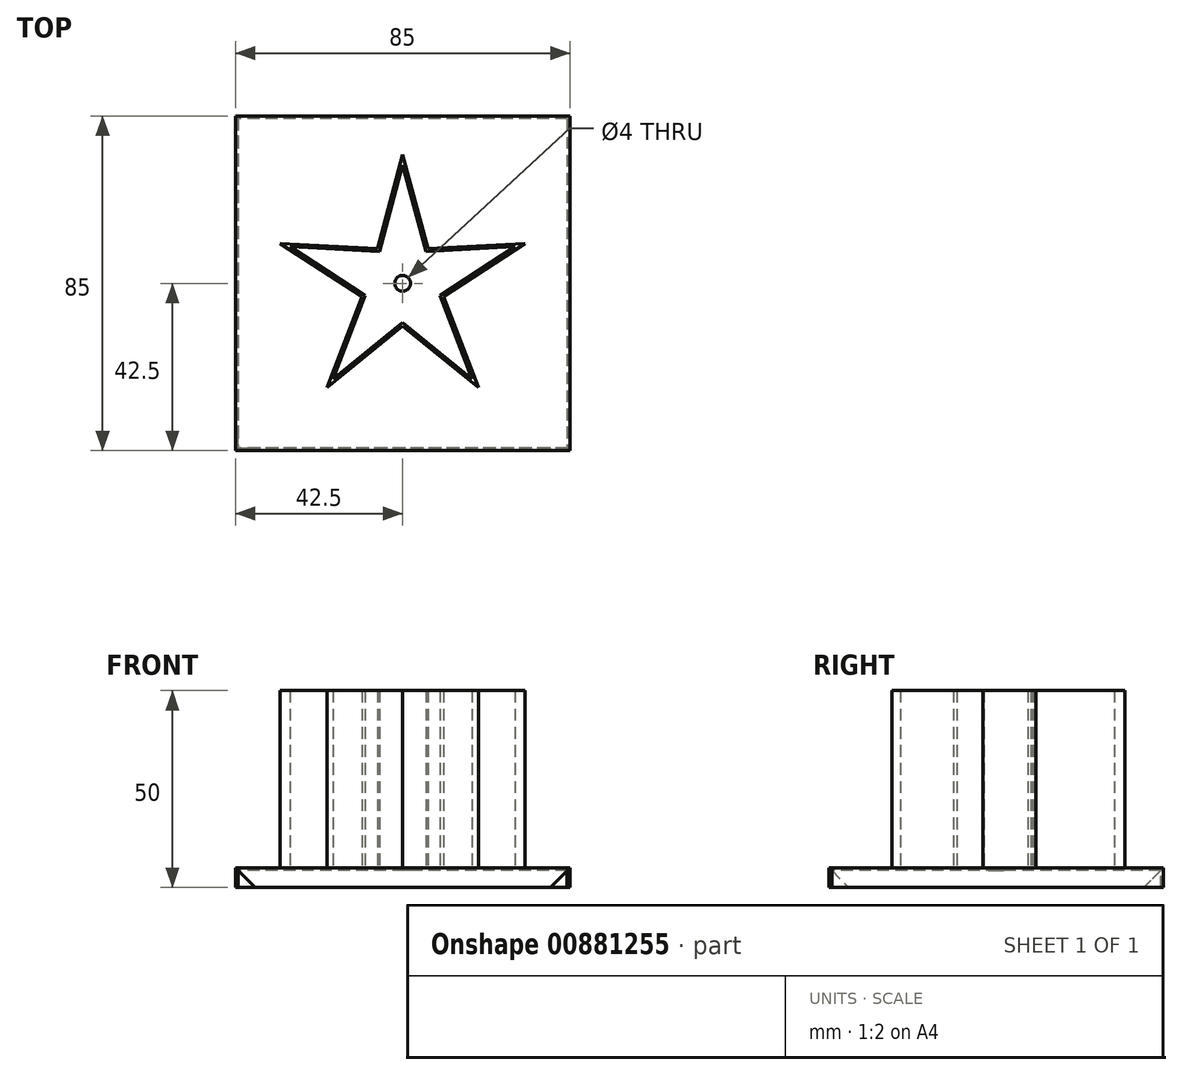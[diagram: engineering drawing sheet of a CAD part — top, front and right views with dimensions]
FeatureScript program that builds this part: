
annotation { "Feature Type Name" : "Feature", "Feature Type Description" : "" }
export const myFeature = defineFeature(function(context is Context, id is Id, definition is map)
    precondition{}
    {
        {
            var Q0;
            Q0=qCreatedBy(makeId("Top.planeOp"),FACE);
            var sketch = newSketch(context, id + "F0", { "sketchPlane" : qUnion([Q0])});
            skLineSegment(sketch, "E0.bottom", {"start": v(42.5, 42.5) * mm, "end": v(-42.5, 42.5) * mm});
            skLineSegment(sketch, "E0.top", {"start": v(42.5, -42.5) * mm, "end": v(-42.5, -42.5) * mm});
            skLineSegment(sketch, "E0.left", {"start": v(42.5, 42.5) * mm, "end": v(42.5, -42.5) * mm});
            skLineSegment(sketch, "E0.right", {"start": v(-42.5, 42.5) * mm, "end": v(-42.5, -42.5) * mm});
            skPoint(sketch, "E0.middle", {"position": v(0, 0) * mm});
            skCircle(sketch, "E1", {"center": v(0, 0) * mm, "radius": 2 * mm});
            skSolve(sketch);
        }
        {
            var Q0;
            Q0 = qSketchRegion(id + "F0", true);
            extrude(context, id + "F1", {"entities" : qUnion([Q0]), "depth" : 0.7 * mm, "offsetDistance" : 25 * mm});
        }
        {
            var Q0;
            Q0=makeQuery(id+"F1.opExtrude","CAP_FACE",FACE,{"disambiguationData":[OSD([sQuery(id+"F0.wireOp",EDGE,"E0.bottom"),sQuery(id+"F0.wireOp",EDGE,"E0.top"),sQuery(id+"F0.wireOp",EDGE,"E0.left"),sQuery(id+"F0.wireOp",EDGE,"E0.right"),sQuery(id+"F0.wireOp",EDGE,"E1")])],"isStart":false});
            var sketch = newSketch(context, id + "F2", { "sketchPlane" : qUnion([Q0])});
            skLineSegment(sketch, "E2", {"start": v(0, 30.03) * mm, "end": v(-5.88, 8.1) * mm});
            skLineSegment(sketch, "E3", {"start": v(-5.88, 8.1) * mm, "end": v(-28.56, 9.28) * mm});
            skLineSegment(sketch, "E4", {"start": v(-28.56, 9.28) * mm, "end": v(-9.51, -3.1) * mm});
            skLineSegment(sketch, "E5", {"start": v(-9.51, -3.1) * mm, "end": v(-17.65, -24.3) * mm});
            skCircle(sketch, "E6", {"center": v(0, 0) * mm, "radius": 10 * mm, "construction": true});
            skLineSegment(sketch, "E7", {"start": v(-17.65, -24.3) * mm, "end": v(0, -10) * mm});
            skLineSegment(sketch, "E8.MirrorCS", {"start": v(17.65, -24.3) * mm, "end": v(0, -10) * mm});
            skLineSegment(sketch, "E9.MirrorCS", {"start": v(9.51, -3.1) * mm, "end": v(17.65, -24.3) * mm});
            skLineSegment(sketch, "E10.MirrorCS", {"start": v(28.56, 9.28) * mm, "end": v(9.51, -3.1) * mm});
            skLineSegment(sketch, "E11.MirrorCS", {"start": v(0, 30.03) * mm, "end": v(5.88, 8.1) * mm});
            skLineSegment(sketch, "E12.MirrorCS", {"start": v(5.88, 8.1) * mm, "end": v(28.56, 9.28) * mm});
            skLineSegment(sketch, "E13.0", {"start": v(0, 32.73) * mm, "end": v(6.4, 8.82) * mm});
            skLineSegment(sketch, "E13.1", {"start": v(6.4, 8.82) * mm, "end": v(31.13, 10.11) * mm});
            skLineSegment(sketch, "E13.2", {"start": v(0, 32.73) * mm, "end": v(-6.4, 8.82) * mm});
            skLineSegment(sketch, "E13.3", {"start": v(31.13, 10.11) * mm, "end": v(10.37, -3.37) * mm});
            skLineSegment(sketch, "E13.4", {"start": v(10.37, -3.37) * mm, "end": v(19.24, -26.48) * mm});
            skLineSegment(sketch, "E13.5", {"start": v(19.24, -26.48) * mm, "end": v(0, -10.9) * mm});
            skLineSegment(sketch, "E13.6", {"start": v(-6.4, 8.82) * mm, "end": v(-31.13, 10.11) * mm});
            skLineSegment(sketch, "E13.7", {"start": v(-31.13, 10.11) * mm, "end": v(-10.37, -3.37) * mm});
            skLineSegment(sketch, "E13.8", {"start": v(-10.37, -3.37) * mm, "end": v(-19.24, -26.48) * mm});
            skLineSegment(sketch, "E13.9", {"start": v(-19.24, -26.48) * mm, "end": v(0, -10.9) * mm});
            skLineSegment(sketch, "E14", {"start": v(0, 0) * mm, "end": v(17.65, -24.3) * mm, "construction": true});
            skLineSegment(sketch, "E15", {"start": v(0, 0) * mm, "end": v(28.56, 9.28) * mm, "construction": true});
            skLineSegment(sketch, "E16", {"start": v(0, 0) * mm, "end": v(-17.65, -24.3) * mm, "construction": true});
            skLineSegment(sketch, "E17", {"start": v(0, 0) * mm, "end": v(-28.56, 9.28) * mm, "construction": true});
            skLineSegment(sketch, "E18", {"start": v(0, 0) * mm, "end": v(0, 30.03) * mm, "construction": true});
            skPoint(sketch, "E19.orphan", {"position": v(0, -10) * mm});
            skSolve(sketch);
        }
        {
            var Q0;
            Q0 = qSketchRegion(id + "F2", true);
            extrude(context, id + "F3", {"entities" : qUnion([Q0]), "operationType" : NewBodyOperationType.ADD, "depth" : 45 * mm, "offsetDistance" : 25 * mm});
        }
        {
            var Q0;
            Q0=makeQuery(id+"F1.opExtrude","CAP_FACE",FACE,{"disambiguationData":[OSD([sQuery(id+"F0.wireOp",EDGE,"E0.bottom"),sQuery(id+"F0.wireOp",EDGE,"E0.top"),sQuery(id+"F0.wireOp",EDGE,"E0.left"),sQuery(id+"F0.wireOp",EDGE,"E0.right"),sQuery(id+"F0.wireOp",EDGE,"E1")])],"isStart":true});
            var sketch = newSketch(context, id + "F4", { "sketchPlane" : qUnion([Q0])});
            skLineSegment(sketch, "E20.0", {"start": v(42.5, -42.5) * mm, "end": v(-42.5, -42.5) * mm});
            skLineSegment(sketch, "E20.1", {"start": v(42.5, -42.5) * mm, "end": v(42.5, 42.5) * mm});
            skLineSegment(sketch, "E20.2", {"start": v(42.5, 42.5) * mm, "end": v(-42.5, 42.5) * mm});
            skLineSegment(sketch, "E20.3", {"start": v(-42.5, -42.5) * mm, "end": v(-42.5, 42.5) * mm});
            skLineSegment(sketch, "E21.0", {"start": v(-41.8, -41.8) * mm, "end": v(-41.8, 41.8) * mm});
            skLineSegment(sketch, "E21.1", {"start": v(41.8, -41.8) * mm, "end": v(-41.8, -41.8) * mm});
            skLineSegment(sketch, "E21.2", {"start": v(41.8, -41.8) * mm, "end": v(41.8, 41.8) * mm});
            skLineSegment(sketch, "E21.3", {"start": v(41.8, 41.8) * mm, "end": v(-41.8, 41.8) * mm});
            skSolve(sketch);
        }
        {
            var Q0;
            Q0 = qSketchRegion(id + "F4", true);
            extrude(context, id + "F5", {"entities" : qUnion([Q0]), "operationType" : NewBodyOperationType.ADD, "depth" : 4.3 * mm, "offsetDistance" : 25 * mm});
        }
        {
            var Q0;
            Q0=makeQuery(id+"F5.opExtrude","SWEPT_FACE",FACE,{"disambiguationData":[OSD([sQuery(id+"F4.wireOp",EDGE,"E21.0")])]});
            var sketch = newSketch(context, id + "F6", { "sketchPlane" : qUnion([Q0])});
            skLineSegment(sketch, "E22.0", {"start": v(42.5, 0.7) * mm, "end": v(42.5, -4.3) * mm});
            skLineSegment(sketch, "E22.1", {"start": v(-42.5, 0.7) * mm, "end": v(-42.5, -4.3) * mm});
            skLineSegment(sketch, "E23", {"start": v(-42.5, 0.7) * mm, "end": v(-37.5, -4.3) * mm});
            skLineSegment(sketch, "E24", {"start": v(-37.5, -4.3) * mm, "end": v(-42.5, -4.3) * mm});
            skLineSegment(sketch, "E25", {"start": v(42.5, 0.7) * mm, "end": v(37.5, -4.3) * mm});
            skPoint(sketch, "E25.endSnap0", {"position": v(-40, -4.3) * mm});
            skLineSegment(sketch, "E26", {"start": v(37.5, -4.3) * mm, "end": v(42.5, -4.3) * mm});
            skSolve(sketch);
        }
        {
            var Q0;
            Q0 = qSketchRegion(id + "F6", true);
            extrude(context, id + "F7", {"entities" : qUnion([Q0]), "operationType" : NewBodyOperationType.REMOVE, "oppositeDirection" : true, "depth" : 25 * mm, "offsetDistance" : 25 * mm});
        }
        {
            var Q0;
            Q0=makeQuery(id+"F5.opExtrude","SWEPT_FACE",FACE,{"disambiguationData":[OSD([sQuery(id+"F4.wireOp",EDGE,"E21.3")])]});
            var sketch = newSketch(context, id + "F8", { "sketchPlane" : qUnion([Q0])});
            skLineSegment(sketch, "E27.0", {"start": v(42.5, 0.7) * mm, "end": v(42.5, -4.3) * mm});
            skLineSegment(sketch, "E27.1", {"start": v(-42.5, -4.3) * mm, "end": v(-42.5, 0.7) * mm});
            skLineSegment(sketch, "E28", {"start": v(-42.5, 0.7) * mm, "end": v(-37.5, -4.3) * mm});
            skLineSegment(sketch, "E29", {"start": v(-37.5, -4.3) * mm, "end": v(-42.5, -4.3) * mm});
            skLineSegment(sketch, "E30", {"start": v(42.5, 0.7) * mm, "end": v(37.5, -4.3) * mm});
            skLineSegment(sketch, "E31", {"start": v(37.5, -4.3) * mm, "end": v(42.5, -4.3) * mm});
            skSolve(sketch);
        }
        {
            var Q0;
            Q0 = qSketchRegion(id + "F8", true);
            var Q1;
            Q1=makeQuery(id+"F5.boolean.opBoolean","MERGE",FACE,{"derivedFrom":[makeQuery(id+"F1.opExtrude","SWEPT_FACE",FACE,{"disambiguationData":[OSD([sQuery(id+"F0.wireOp",EDGE,"E0.top")])]}),makeQuery(id+"F5.opExtrude","SWEPT_FACE",FACE,{"disambiguationData":[OSD([sQuery(id+"F4.wireOp",EDGE,"E20.2")])]})]});
            extrude(context, id + "F9", {"entities" : qUnion([Q0]), "operationType" : NewBodyOperationType.REMOVE, "oppositeDirection" : true, "depth" : 25 * mm, "endBoundEntityFace" : qUnion([Q1]), "offsetDistance" : 25 * mm});
        }
    });
